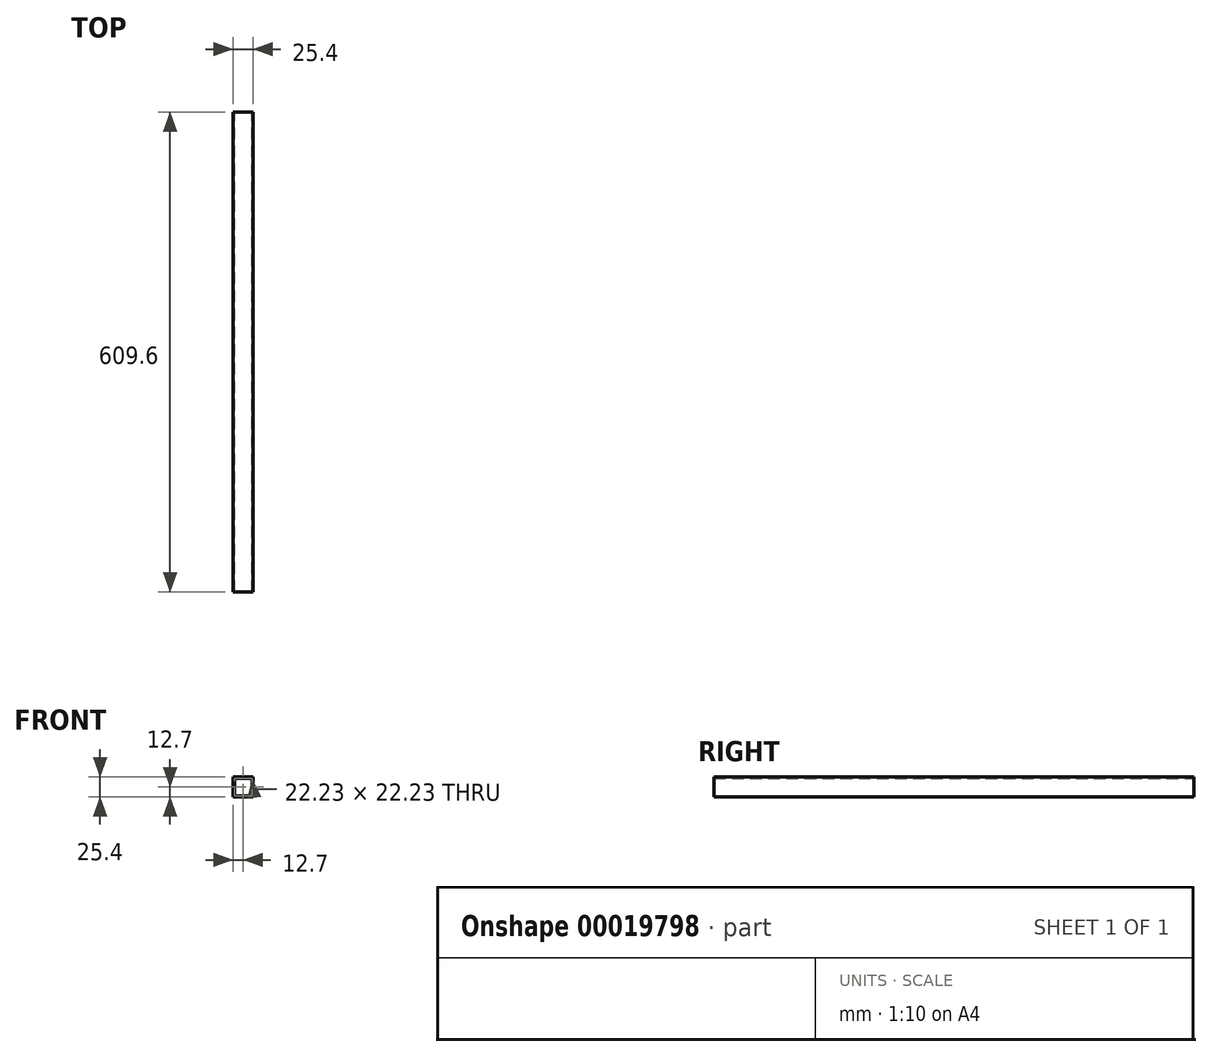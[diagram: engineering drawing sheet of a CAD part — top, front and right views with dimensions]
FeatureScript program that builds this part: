
annotation { "Feature Type Name" : "Feature", "Feature Type Description" : "" }
export const myFeature = defineFeature(function(context is Context, id is Id, definition is map)
    precondition{}
    {
        {
            var Q0;
            Q0=qCreatedBy(makeId("Front.planeOp"),FACE);
            var sketch = newSketch(context, id + "F0", { "sketchPlane" : qUnion([Q0])});
            skLineSegment(sketch, "E0.rect.bottom", {"start": v(12.7, 12.7) * mm, "end": v(-12.7, 12.7) * mm});
            skLineSegment(sketch, "E0.rect.top", {"start": v(12.7, -12.7) * mm, "end": v(-12.7, -12.7) * mm});
            skLineSegment(sketch, "E0.rect.left", {"start": v(12.7, 12.7) * mm, "end": v(12.7, -12.7) * mm});
            skLineSegment(sketch, "E0.rect.right", {"start": v(-12.7, 12.7) * mm, "end": v(-12.7, -12.7) * mm});
            skPoint(sketch, "E0.rect.middle", {"position": v(0, 0) * mm});
            skLineSegment(sketch, "E1.rect.bottom", {"start": v(11.11, 11.11) * mm, "end": v(-11.11, 11.11) * mm});
            skLineSegment(sketch, "E1.rect.top", {"start": v(11.11, -11.11) * mm, "end": v(-11.11, -11.11) * mm});
            skLineSegment(sketch, "E1.rect.left", {"start": v(11.11, 11.11) * mm, "end": v(11.11, -11.11) * mm});
            skLineSegment(sketch, "E1.rect.right", {"start": v(-11.11, 11.11) * mm, "end": v(-11.11, -11.11) * mm});
            skSolve(sketch);
        }
        {
            var Q0;
            Q0=makeQuery(id+"F0.imprint","IMPRINT",FACE,{"disambiguationData":[TD([[makeQuery(id+"F0.imprint","IMPRINT",EDGE,{"derivedFrom":sQuery(id+"F0.wireOp",EDGE,"E0.rect.bottom")}),1.0]])]});
            extrude(context, id + "F1", {"entities" : qUnion([Q0]), "endBound" : BoundingType.SYMMETRIC, "depth" : 609.6 * mm});
        }
    });
